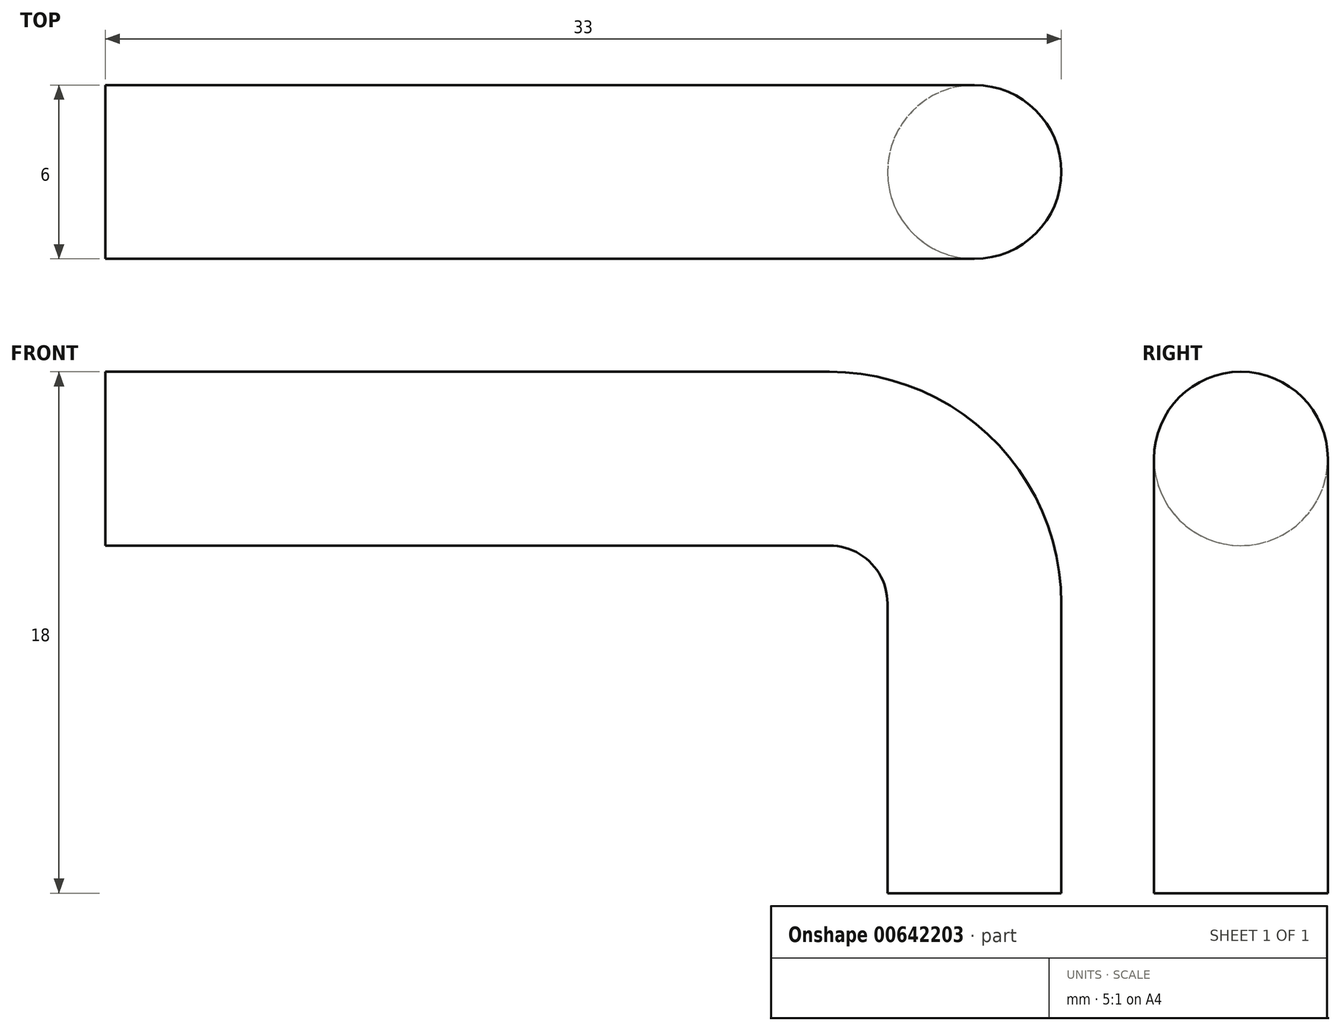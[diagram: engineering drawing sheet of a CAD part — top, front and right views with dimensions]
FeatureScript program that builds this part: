
annotation { "Feature Type Name" : "Feature", "Feature Type Description" : "" }
export const myFeature = defineFeature(function(context is Context, id is Id, definition is map)
    precondition{}
    {
        {
            var Q0;
            Q0=qCreatedBy(makeId("Front.planeOp"),FACE);
            var sketch = newSketch(context, id + "F0", { "sketchPlane" : qUnion([Q0])});
            skLineSegment(sketch, "E0", {"start": v(0, 0) * mm, "end": v(25, 0) * mm});
            skLineSegment(sketch, "E1", {"start": v(30, -5) * mm, "end": v(30, -15) * mm});
            skPoint(sketch, "E2.visualSharp", {"position": v(30, 0) * mm});
            skArc(sketch, "E2.filletArc", {"start": v(30, -5) * mm, "mid": v(28.54, -1.46) * mm, "end": v(25, 0) * mm});
            skSolve(sketch);
        }
        {
            var Q0;
            Q0=qCreatedBy(makeId("Right.planeOp"),FACE);
            var sketch = newSketch(context, id + "F1", { "sketchPlane" : qUnion([Q0])});
            skCircle(sketch, "E3", {"center": v(0, 0) * mm, "radius": 3 * mm});
            skSolve(sketch);
        }
        {
            var Q0;
            Q0 = qSketchRegion(id + "F1", true);
            var Q1;
            Q1 = qConstructionFilter(qBodyType(qCreatedBy(id + "F0" ,EDGE), BodyType.WIRE), ConstructionObject.NO);
            sweep(context, id + "F2", {"profiles" : qUnion([Q0]), "path" : qUnion([Q1])});
        }
    });
